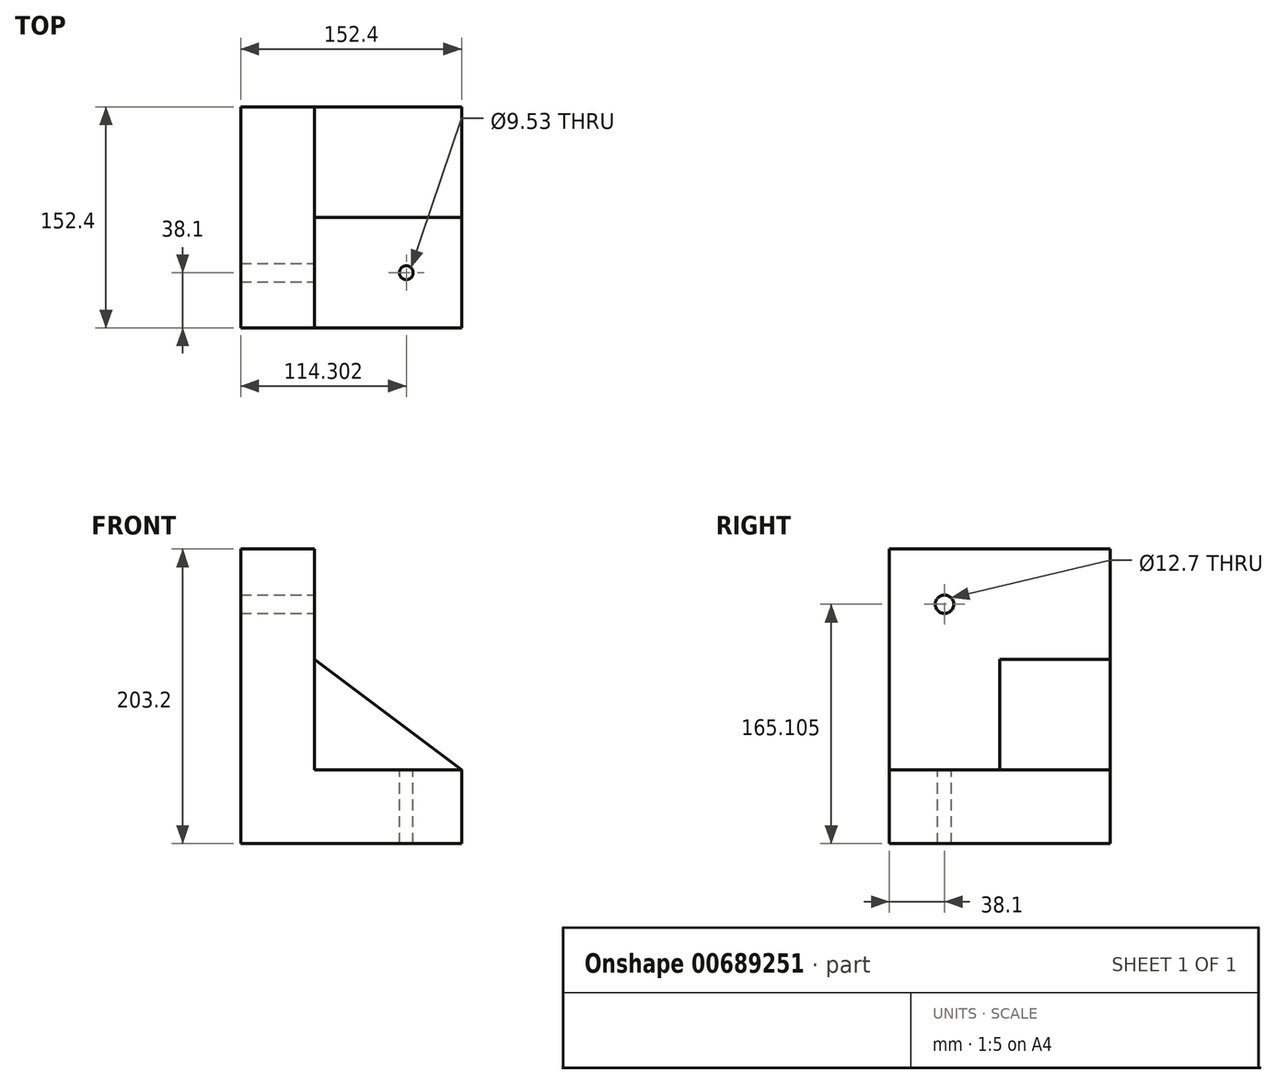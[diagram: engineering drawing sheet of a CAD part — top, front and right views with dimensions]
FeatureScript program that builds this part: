
annotation { "Feature Type Name" : "Feature", "Feature Type Description" : "" }
export const myFeature = defineFeature(function(context is Context, id is Id, definition is map)
    precondition{}
    {
        {
            var Q0;
            Q0=qCreatedBy(makeId("Front.planeOp"),FACE);
            var sketch = newSketch(context, id + "F0", { "sketchPlane" : qUnion([Q0])});
            skLineSegment(sketch, "E0", {"start": v(-46.88, 106.47) * mm, "end": v(-46.88, -96.73) * mm});
            skLineSegment(sketch, "E1", {"start": v(-46.88, -96.73) * mm, "end": v(105.52, -96.73) * mm});
            skLineSegment(sketch, "E2", {"start": v(105.52, -96.73) * mm, "end": v(105.52, -45.93) * mm});
            skLineSegment(sketch, "E3", {"start": v(-46.88, 106.47) * mm, "end": v(3.92, 106.47) * mm});
            skLineSegment(sketch, "E4", {"start": v(3.92, 106.47) * mm, "end": v(3.92, -45.93) * mm});
            skLineSegment(sketch, "E5", {"start": v(105.52, -45.93) * mm, "end": v(3.92, -45.93) * mm});
            skSolve(sketch);
        }
        {
            var Q0;
            Q0=makeQuery(id+"F0.imprint","IMPRINT",FACE,{"disambiguationData":[TD([[makeQuery(id+"F0.imprint","IMPRINT",EDGE,{"derivedFrom":sQuery(id+"F0.wireOp",EDGE,"E0")}),1.0]])]});
            extrude(context, id + "F1", {"entities" : qUnion([Q0]), "depth" : 152.4 * mm, "offsetDistance" : 25.4 * mm});
        }
        {
            var Q0;
            Q0=makeQuery(id+"F1.opExtrude","SWEPT_FACE",FACE,{"disambiguationData":[OSD([sQuery(id+"F0.wireOp",EDGE,"E5")])]});
            var sketch = newSketch(context, id + "F2", { "sketchPlane" : qUnion([Q0])});
            skLineSegment(sketch, "E6.bottom", {"start": v(3.92, 0) * mm, "end": v(105.52, 0) * mm});
            skLineSegment(sketch, "E6.top", {"start": v(3.92, -76.2) * mm, "end": v(105.52, -76.2) * mm});
            skLineSegment(sketch, "E6.left", {"start": v(3.92, 0) * mm, "end": v(3.92, -76.2) * mm});
            skLineSegment(sketch, "E6.right", {"start": v(105.52, 0) * mm, "end": v(105.52, -76.2) * mm});
            skSolve(sketch);
        }
        {
            var Q0;
            Q0=makeQuery(id+"F2.imprint","IMPRINT",FACE,{"disambiguationData":[TD([[makeQuery(id+"F2.imprint","IMPRINT",EDGE,{"derivedFrom":sQuery(id+"F2.wireOp",EDGE,"E6.bottom")}),1.0]])]});
            extrude(context, id + "F3", {"entities" : qUnion([Q0]), "operationType" : NewBodyOperationType.ADD, "depth" : 76.2 * mm, "offsetDistance" : 25.4 * mm});
        }
        {
            var Q0;
            Q0=makeQuery(id+"F3.opExtrude","SWEPT_FACE",FACE,{"disambiguationData":[OSD([sQuery(id+"F2.wireOp",EDGE,"E6.top")])]});
            var sketch = newSketch(context, id + "F4", { "sketchPlane" : qUnion([Q0])});
            skLineSegment(sketch, "E7", {"start": v(3.92, 30.27) * mm, "end": v(105.52, -45.93) * mm});
            skLineSegment(sketch, "E8", {"start": v(105.52, 30.27) * mm, "end": v(105.52, -45.93) * mm});
            skLineSegment(sketch, "E9", {"start": v(105.52, 30.27) * mm, "end": v(3.92, 30.27) * mm});
            skSolve(sketch);
        }
        {
            var Q0;
            Q0=makeQuery(id+"F4.imprint","IMPRINT",FACE,{"disambiguationData":[TD([[makeQuery(id+"F4.imprint","IMPRINT",EDGE,{"derivedFrom":sQuery(id+"F4.wireOp",EDGE,"E7")}),1.0]])]});
            extrude(context, id + "F5", {"entities" : qUnion([Q0]), "operationType" : NewBodyOperationType.REMOVE, "oppositeDirection" : true, "depth" : 76.2 * mm, "offsetDistance" : 25.4 * mm});
        }
        {
            var Q0;
            Q0=makeQuery(id+"F1.opExtrude","SWEPT_FACE",FACE,{"disambiguationData":[OSD([sQuery(id+"F0.wireOp",EDGE,"E5")])]});
            var sketch = newSketch(context, id + "F6", { "sketchPlane" : qUnion([Q0])});
            skCircle(sketch, "E10", {"center": v(67.42, -114.3) * mm, "radius": 4.76 * mm});
            skSolve(sketch);
        }
        {
            var Q0;
            Q0=sQuery(id+"F6.wireOp",VERTEX,"E10.center");
            var Q1;
            Q1=makeQuery(id+"F1.opExtrude","SWEPT_BODY",BODY,{"disambiguationData":[OSD([sQuery(id+"F0.wireOp",EDGE,"E0"),sQuery(id+"F0.wireOp",EDGE,"E1"),sQuery(id+"F0.wireOp",EDGE,"E2"),sQuery(id+"F0.wireOp",EDGE,"E3"),sQuery(id+"F0.wireOp",EDGE,"E4"),sQuery(id+"F0.wireOp",EDGE,"E5")])]});
            hole(context, id + "F7", {"style" : HoleStyle.SIMPLE, "endStyle" : HoleEndStyle.THROUGH, "holeDiameter" : 9.52 * mm, "majorDiameter" : 6.35 * mm, "isTappedThrough" : true, "tappedDepth" : 12.7 * mm, "tapClearance" : 3, "locations" : qUnion([Q0]), "scope" : qUnion([Q1])});
        }
        {
            var Q0;
            Q0=makeQuery(id+"F1.opExtrude","SWEPT_FACE",FACE,{"disambiguationData":[OSD([sQuery(id+"F0.wireOp",EDGE,"E4")])]});
            var sketch = newSketch(context, id + "F8", { "sketchPlane" : qUnion([Q0])});
            skPoint(sketch, "E11", {"position": v(-114.3, 68.37) * mm});
            skPoint(sketch, "E12", {"position": v(82.47, -105.82) * mm});
            skSolve(sketch);
        }
        {
            var Q0;
            Q0=sQuery(id+"F8.wireOp",VERTEX,"E11");
            var Q1;
            Q1=makeQuery(id+"F1.opExtrude","SWEPT_BODY",BODY,{"disambiguationData":[OSD([sQuery(id+"F0.wireOp",EDGE,"E0"),sQuery(id+"F0.wireOp",EDGE,"E1"),sQuery(id+"F0.wireOp",EDGE,"E2"),sQuery(id+"F0.wireOp",EDGE,"E3"),sQuery(id+"F0.wireOp",EDGE,"E4"),sQuery(id+"F0.wireOp",EDGE,"E5")])]});
            hole(context, id + "F9", {"style" : HoleStyle.SIMPLE, "endStyle" : HoleEndStyle.THROUGH, "holeDiameter" : 12.7 * mm, "majorDiameter" : 6.35 * mm, "isTappedThrough" : true, "tappedDepth" : 12.7 * mm, "tapClearance" : 3, "locations" : qUnion([Q0]), "scope" : qUnion([Q1])});
        }
    });
